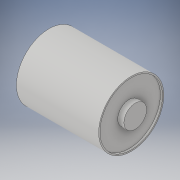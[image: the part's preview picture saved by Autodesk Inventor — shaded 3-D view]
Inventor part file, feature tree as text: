
AUTODESK INVENTOR PART (.ipt)
format: ipt  version: 2019 (Build 230136000, 136)  size: 128,512 bytes
history: native  units: mm
features: sketch x5, extrude x4, other x1, hole x1
ambient origin geometry x8: Origin, YZ Plane, XZ Plane, XY Plane, X Axis, Y Axis, Z Axis, Center Point
bodies: Body1 (feature_tree)
feature tree (11):
  other  "Bryła1"
  extrude  "Wyciągnięcie proste1"  Depth=24.4mm
  extrude  "Wyciągnięcie proste2"  Depth=30.8mm TaperAngle=0.0deg
  extrude  "Wyciągnięcie proste3"  Depth=23.4mm
  hole  "Otwór1"  [1 undecoded]
  extrude  "Wyciągnięcie proste4"  Depth=2.3mm TaperAngle=0.0deg
  sketch  "Szkic1"
  sketch  "Szkic2"
  sketch  "Szkic3"
  sketch  "Szkic4"
  sketch  "Szkic5"
note: 1 required parameter value undecoded (feature->parameter linkage not recoverable at this tier; creation-order binding heuristic only, values carry confidence <= 0.55)
